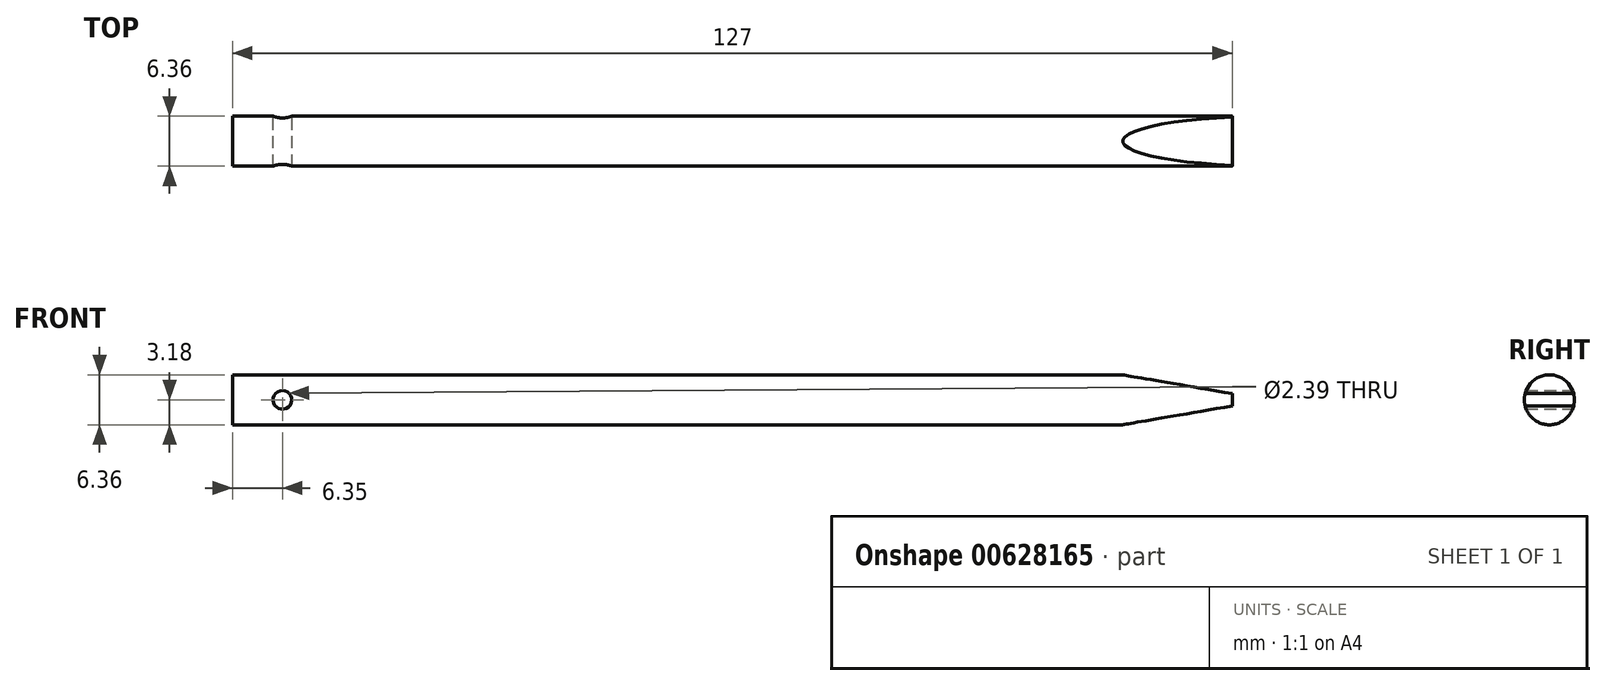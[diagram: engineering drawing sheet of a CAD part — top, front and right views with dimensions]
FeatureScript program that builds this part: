
annotation { "Feature Type Name" : "Feature", "Feature Type Description" : "" }
export const myFeature = defineFeature(function(context is Context, id is Id, definition is map)
    precondition{}
    {
        {
            var Q0;
            Q0=qCreatedBy(makeId("Right.planeOp"),FACE);
            var sketch = newSketch(context, id + "F0", { "sketchPlane" : qUnion([Q0])});
            skCircle(sketch, "E0", {"center": v(0, 0) * mm, "radius": 3.18 * mm});
            skSolve(sketch);
        }
        {
            var Q0;
            Q0=makeQuery(id+"F0.imprint","IMPRINT",FACE,{"disambiguationData":[TD([[makeQuery(id+"F0.imprint","IMPRINT",EDGE,{"derivedFrom":sQuery(id+"F0.wireOp",EDGE,"E0")}),1.0]])]});
            extrude(context, id + "F1", {"entities" : qUnion([Q0]), "oppositeDirection" : true, "depth" : 127 * mm, "offsetDistance" : 25.4 * mm});
        }
        {
            var Q0;
            Q0=qCreatedBy(makeId("Front.planeOp"),FACE);
            var sketch = newSketch(context, id + "F2", { "sketchPlane" : qUnion([Q0])});
            skLineSegment(sketch, "E1", {"start": v(0, 0.78) * mm, "end": v(-16.09, 3.54) * mm});
            skLineSegment(sketch, "E2", {"start": v(-16.09, 3.54) * mm, "end": v(-16.09, 4.48) * mm});
            skLineSegment(sketch, "E3", {"start": v(-16.09, 4.48) * mm, "end": v(0, 4.48) * mm});
            skLineSegment(sketch, "E4", {"start": v(0, 4.48) * mm, "end": v(0, 0.78) * mm});
            skLineSegment(sketch, "E5", {"start": v(0, 0) * mm, "end": v(-18.7, 0) * mm, "construction": true});
            skLineSegment(sketch, "E6.MirrorCS", {"start": v(-16.09, -3.54) * mm, "end": v(-16.09, -4.48) * mm});
            skLineSegment(sketch, "E7.MirrorCS", {"start": v(0, -0.78) * mm, "end": v(-16.09, -3.54) * mm});
            skLineSegment(sketch, "E8.MirrorCS", {"start": v(0, -4.48) * mm, "end": v(0, -0.78) * mm});
            skLineSegment(sketch, "E9.MirrorCS", {"start": v(-16.09, -4.48) * mm, "end": v(0, -4.48) * mm});
            skCircle(sketch, "E10", {"center": v(-120.65, 0) * mm, "radius": 1.2 * mm});
            skSolve(sketch);
        }
        {
            var Q0;
            Q0 = qSketchRegion(id + "F2", true);
            extrude(context, id + "F3", {"entities" : qUnion([Q0]), "operationType" : NewBodyOperationType.REMOVE, "endBound" : BoundingType.SYMMETRIC, "depth" : 25.4 * mm, "offsetDistance" : 25.4 * mm});
        }
    });
